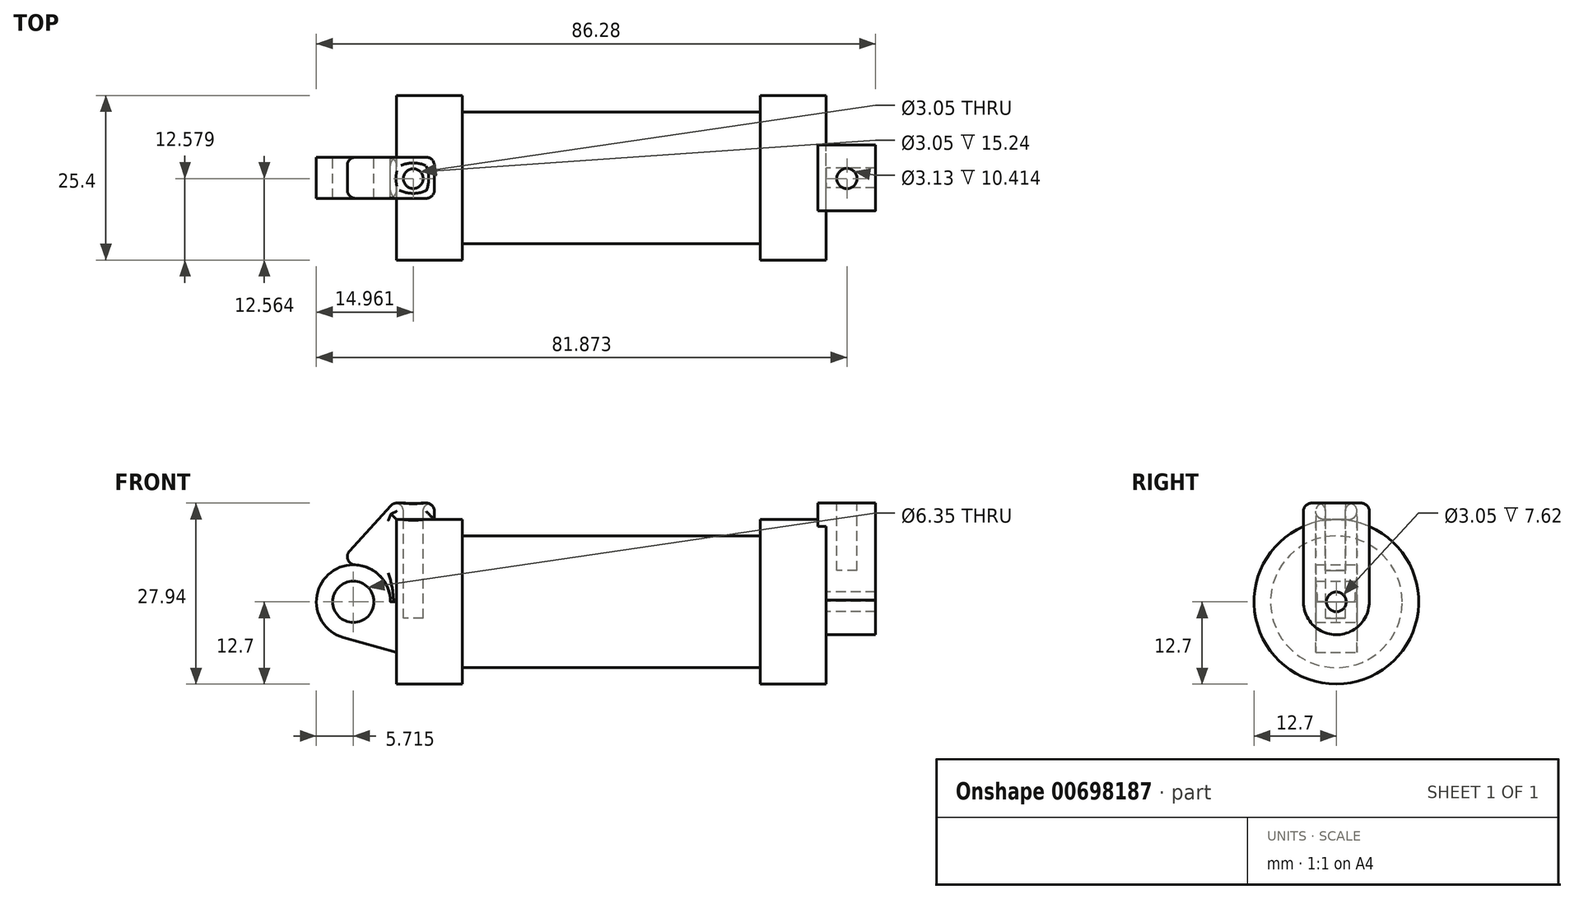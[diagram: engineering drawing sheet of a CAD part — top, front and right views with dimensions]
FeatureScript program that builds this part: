
annotation { "Feature Type Name" : "Feature", "Feature Type Description" : "" }
export const myFeature = defineFeature(function(context is Context, id is Id, definition is map)
    precondition{}
    {
        {
            var Q0;
            Q0=qCreatedBy(makeId("Front.planeOp"),FACE);
            var sketch = newSketch(context, id + "F0", { "sketchPlane" : qUnion([Q0])});
            skLineSegment(sketch, "E0", {"start": v(0, 0) * mm, "end": v(0, 12.7) * mm});
            skLineSegment(sketch, "E1", {"start": v(0, 12.7) * mm, "end": v(10.16, 12.7) * mm});
            skLineSegment(sketch, "E2", {"start": v(10.16, 12.7) * mm, "end": v(10.16, 10.16) * mm});
            skLineSegment(sketch, "E3", {"start": v(10.16, 10.16) * mm, "end": v(56.13, 10.16) * mm});
            skLineSegment(sketch, "E4", {"start": v(56.13, 10.16) * mm, "end": v(56.13, 12.7) * mm});
            skLineSegment(sketch, "E5", {"start": v(56.13, 12.7) * mm, "end": v(66.3, 12.7) * mm});
            skLineSegment(sketch, "E6", {"start": v(66.3, 12.7) * mm, "end": v(66.3, 0) * mm});
            skLineSegment(sketch, "E7", {"start": v(66.3, 0) * mm, "end": v(0, 0) * mm});
            skLineSegment(sketch, "E8", {"start": v(5.84, 15.24) * mm, "end": v(-0.5, 15.24) * mm});
            skLineSegment(sketch, "E9", {"start": v(-0.5, 15.24) * mm, "end": v(-10.88, 3.85) * mm});
            skLineSegment(sketch, "E10", {"start": v(0, 0) * mm, "end": v(-6.65, 0) * mm});
            skCircle(sketch, "E11", {"center": v(-6.65, 0) * mm, "radius": 5.72 * mm});
            skCircle(sketch, "E12", {"center": v(-6.65, 0) * mm, "radius": 3.18 * mm});
            skLineSegment(sketch, "E13", {"start": v(5.84, 15.24) * mm, "end": v(5.84, -9.4) * mm});
            skLineSegment(sketch, "E14", {"start": v(5.84, -9.4) * mm, "end": v(-8.18, -5.5) * mm});
            skSolve(sketch);
        }
        {
            var Q0;
            {var subQ0=sQuery(id+"F0.wireOp",EDGE,"E2");Q0=makeQuery(id+"F0.imprint","IMPRINT",FACE,{"disambiguationData":[TD([[makeQuery(id+"F0.imprint","IMPRINT",EDGE,{"derivedFrom":subQ0}),-1.0]])]});}
            var Q1;
            {var subQ0=sQuery(id+"F0.wireOp",EDGE,"E0");Q1=makeQuery(id+"F0.imprint","IMPRINT",FACE,{"disambiguationData":[TD([[makeQuery(id+"F0.imprint","IMPRINT",EDGE,{"derivedFrom":subQ0}),-1.0]])]});}
            var Q2;
            Q2=sQuery(id+"F0.wireOp",EDGE,"E7");
            revolve(context, id + "F1", {"entities" : qUnion([Q0, Q1]), "axis" : qUnion([Q2]), "revolveType" : RevolveType.FULL});
        }
        {
            var Q0;
            {var subQ5=sQuery(id+"F0.wireOp",EDGE,"E12");Q0=makeQuery(id+"F0.imprint","IMPRINT",FACE,{"disambiguationData":[TD([[makeQuery(id+"F0.imprint","IMPRINT",EDGE,{"derivedFrom":subQ5}),-1.0]])]});}
            var Q1;
            {var subQ0=sQuery(id+"F0.wireOp",EDGE,"E14");Q1=makeQuery(id+"F0.imprint","IMPRINT",FACE,{"disambiguationData":[TD([[makeQuery(id+"F0.imprint","IMPRINT",EDGE,{"derivedFrom":subQ0}),-1.0]])]});}
            extrude(context, id + "F2", {"entities" : qUnion([Q0, Q1]), "operationType" : NewBodyOperationType.ADD, "endBound" : BoundingType.SYMMETRIC, "depth" : 6.35 * mm, "offsetDistance" : 25.4 * mm});
        }
        {
            var Q0;
            {var subQ1=sQuery(id+"F0.wireOp",EDGE,"E0");Q0=makeQuery(id+"F0.imprint","IMPRINT",FACE,{"disambiguationData":[TD([[makeQuery(id+"F0.imprint","IMPRINT",EDGE,{"derivedFrom":subQ1}),1.0]])]});}
            extrude(context, id + "F3", {"entities" : qUnion([Q0]), "endBound" : BoundingType.SYMMETRIC, "depth" : 6.35 * mm, "offsetDistance" : 25.4 * mm});
        }
        {
            var Q0;
            Q0=makeQuery(id+"F1.opRevolve","SWEPT_FACE",FACE,{"disambiguationData":[OSD([sQuery(id+"F0.wireOp",EDGE,"E6")])]});
            var sketch = newSketch(context, id + "F4", { "sketchPlane" : qUnion([Q0])});
            skCircle(sketch, "E15", {"center": v(0, 0) * mm, "radius": 1.52 * mm});
            skCircle(sketch, "E16", {"center": v(0, 0) * mm, "radius": 5.08 * mm});
            skLineSegment(sketch, "E17", {"start": v(-5.07, 0.25) * mm, "end": v(-5.07, 13.97) * mm});
            skLineSegment(sketch, "E18", {"start": v(5.08, 0.05) * mm, "end": v(5.08, 13.97) * mm});
            skLineSegment(sketch, "E19", {"start": v(-3.8, 15.24) * mm, "end": v(3.8, 15.24) * mm});
            skPoint(sketch, "E20.visualSharp", {"position": v(-5.07, 15.24) * mm});
            skArc(sketch, "E20.filletArc", {"start": v(-3.8, 15.24) * mm, "mid": v(-4.7, 14.87) * mm, "end": v(-5.07, 13.97) * mm});
            skPoint(sketch, "E21.visualSharp", {"position": v(5.08, 15.24) * mm});
            skArc(sketch, "E21.filletArc", {"start": v(5.08, 13.97) * mm, "mid": v(4.7, 14.87) * mm, "end": v(3.8, 15.24) * mm});
            skSolve(sketch);
        }
        {
            var Q0;
            Q0=makeQuery(id+"F4.imprint","IMPRINT",FACE,{"disambiguationData":[TD([[makeQuery(id+"F4.imprint","IMPRINT",EDGE,{"derivedFrom":sQuery(id+"F4.wireOp",EDGE,"E15")}),-1.0]])]});
            var Q1;
            {var subQ0=sQuery(id+"F4.wireOp",EDGE,"E17");var subQ1=sQuery(id+"F4.wireOp",EDGE,"E16");var subQ2=makeQuery(id+"F4.imprint","INTERSECT",VERTEX,{"derivedFrom":[subQ1,subQ0]});Q1=makeQuery(id+"F4.imprint","IMPRINT",FACE,{"disambiguationData":[TD([[makeQuery(id+"F4.imprint","IMPRINT",EDGE,{"disambiguationData":[TD([[subQ2,1.0]])],"derivedFrom":subQ1}),-1.0]])]});}
            extrude(context, id + "F5", {"entities" : qUnion([Q0, Q1]), "operationType" : NewBodyOperationType.ADD, "depth" : 7.62 * mm, "offsetDistance" : 25.4 * mm});
        }
        {
            var Q0;
            {var subQ0=sQuery(id+"F4.wireOp",EDGE,"E19");Q0=makeQuery(id+"F4.imprint","IMPRINT",FACE,{"disambiguationData":[TD([[makeQuery(id+"F4.imprint","IMPRINT",EDGE,{"derivedFrom":subQ0}),-1.0]])]});}
            extrude(context, id + "F6", {"entities" : qUnion([Q0]), "operationType" : NewBodyOperationType.ADD, "depth" : 7.62 * mm, "offsetDistance" : 25.4 * mm, "hasSecondDirection" : true, "secondDirectionOppositeDirection" : true, "secondDirectionDepth" : 1.27 * mm});
        }
        {
            var Q0;
            Q0=makeQuery(id+"F3.opExtrude","SWEPT_FACE",FACE,{"disambiguationData":[OSD([sQuery(id+"F0.wireOp",EDGE,"E8")])]});
            var sketch = newSketch(context, id + "F7", { "sketchPlane" : qUnion([Q0])});
            skCircle(sketch, "E22", {"center": v(2.6, -0.14) * mm, "radius": 1.52 * mm});
            skCircle(sketch, "E23", {"center": v(69.74, 0.16) * mm, "radius": 1.52 * mm});
            skSolve(sketch);
        }
        {
            var Q0;
            Q0=makeQuery(id+"F7.imprint","IMPRINT",FACE,{"disambiguationData":[TD([[makeQuery(id+"F7.imprint","IMPRINT",EDGE,{"derivedFrom":sQuery(id+"F7.wireOp",EDGE,"E22")}),1.0]])]});
            extrude(context, id + "F8", {"entities" : qUnion([Q0]), "operationType" : NewBodyOperationType.REMOVE, "oppositeDirection" : true, "depth" : 17.78 * mm, "offsetDistance" : 25.4 * mm});
        }
        {
            var Q0;
            Q0=makeQuery(id+"F6.opExtrude","SWEPT_FACE",FACE,{"disambiguationData":[OSD([sQuery(id+"F4.wireOp",EDGE,"E19")])]});
            var sketch = newSketch(context, id + "F9", { "sketchPlane" : qUnion([Q0])});
            skCircle(sketch, "E24", {"center": v(69.5, -0.12) * mm, "radius": 1.57 * mm});
            skSolve(sketch);
        }
        {
            var Q0;
            Q0 = qSketchRegion(id + "F9", true);
            extrude(context, id + "F10", {"entities" : qUnion([Q0]), "operationType" : NewBodyOperationType.REMOVE, "oppositeDirection" : true, "depth" : 10.4 * mm, "offsetDistance" : 25.4 * mm});
        }
        {
            var Q0;
            Q0=makeQuery(id+"F1.opRevolve","SWEPT_FACE",FACE,{"disambiguationData":[OSD([sQuery(id+"F0.wireOp",EDGE,"E2")])]});
            var Q1;
            Q1=makeQuery(id+"F1.opRevolve","SWEPT_FACE",FACE,{"disambiguationData":[OSD([sQuery(id+"F0.wireOp",EDGE,"E3")])]});
            var Q2;
            Q2=makeQuery(id+"F1.opRevolve","SWEPT_EDGE",EDGE,{"disambiguationData":[OSD([sQuery(id+"F0.wireOp",EDGE,"E5"),sQuery(id+"F0.wireOp",EDGE,"E6")])]});
            var Q3;
            Q3=makeQuery(id+"F1.opRevolve","SWEPT_EDGE",EDGE,{"disambiguationData":[OSD([sQuery(id+"F0.wireOp",EDGE,"E4"),sQuery(id+"F0.wireOp",EDGE,"E5")])]});
            var Q4;
            {var subQ0=sQuery(id+"F4.wireOp",EDGE,"E18");var subQ1=sQuery(id+"F4.wireOp",EDGE,"E17");var subQ2=sQuery(id+"F0.wireOp",EDGE,"E6");var subQ3=sQuery(id+"F0.wireOp",EDGE,"E5");Q4=makeQuery(id+"F6.boolean.opBoolean","MERGE",FACE,{"derivedFrom":[makeQuery(id+"F5.opExtrude","CAP_FACE",FACE,{"disambiguationData":[OSD([subQ3,subQ2,sQuery(id+"F4.wireOp",EDGE,"E15"),sQuery(id+"F4.wireOp",EDGE,"E16"),subQ1,subQ0])],"isStart":false}),makeQuery(id+"F6.opExtrude","CAP_FACE",FACE,{"disambiguationData":[OSD([subQ3,subQ2,subQ1,subQ0,sQuery(id+"F4.wireOp",EDGE,"E19"),sQuery(id+"F4.wireOp",EDGE,"E20.filletArc"),sQuery(id+"F4.wireOp",EDGE,"E21.filletArc")])],"isStart":false})]});}
            var Q5;
            Q5=makeQuery(id+"F1.opRevolve","SWEPT_FACE",FACE,{"disambiguationData":[OSD([sQuery(id+"F0.wireOp",EDGE,"E1")])]});
            var Q6;
            Q6=makeQuery(id+"F3.opExtrude","SWEPT_FACE",FACE,{"disambiguationData":[OSD([sQuery(id+"F0.wireOp",EDGE,"E9")])]});
            var Q7;
            Q7=makeQuery(id+"F3.opExtrude","SWEPT_FACE",FACE,{"disambiguationData":[OSD([sQuery(id+"F0.wireOp",EDGE,"E8")])]});
            var Q8;
            Q8=makeQuery(id+"F6.opExtrude","CAP_FACE",FACE,{"disambiguationData":[OSD([sQuery(id+"F0.wireOp",EDGE,"E5"),sQuery(id+"F0.wireOp",EDGE,"E6"),sQuery(id+"F4.wireOp",EDGE,"E17"),sQuery(id+"F4.wireOp",EDGE,"E18"),sQuery(id+"F4.wireOp",EDGE,"E19"),sQuery(id+"F4.wireOp",EDGE,"E20.filletArc"),sQuery(id+"F4.wireOp",EDGE,"E21.filletArc")])],"isStart":true});
            var Q9;
            Q9=makeQuery(id+"F6.opExtrude","SWEPT_FACE",FACE,{"disambiguationData":[OSD([sQuery(id+"F4.wireOp",EDGE,"E19")])]});
            var Q10;
            Q10=makeQuery(id+"F3.opExtrude","CAP_FACE",FACE,{"disambiguationData":[OSD([sQuery(id+"F0.wireOp",EDGE,"E0"),sQuery(id+"F0.wireOp",EDGE,"E1"),sQuery(id+"F0.wireOp",EDGE,"E8"),sQuery(id+"F0.wireOp",EDGE,"E9"),sQuery(id+"F0.wireOp",EDGE,"E10"),sQuery(id+"F0.wireOp",EDGE,"E11"),sQuery(id+"F0.wireOp",EDGE,"E13")])],"isStart":true});
            var Q11;
            Q11=makeQuery(id+"F3.opExtrude","CAP_FACE",FACE,{"disambiguationData":[OSD([sQuery(id+"F0.wireOp",EDGE,"E0"),sQuery(id+"F0.wireOp",EDGE,"E1"),sQuery(id+"F0.wireOp",EDGE,"E8"),sQuery(id+"F0.wireOp",EDGE,"E9"),sQuery(id+"F0.wireOp",EDGE,"E10"),sQuery(id+"F0.wireOp",EDGE,"E11"),sQuery(id+"F0.wireOp",EDGE,"E13")])],"isStart":false});
            var Q12;
            Q12=makeQuery(id+"F2.opExtrude","CAP_EDGE",EDGE,{"disambiguationData":[OSD([sQuery(id+"F0.wireOp",EDGE,"E11")])],"isStart":false});
            var Q13;
            Q13=makeQuery(id+"F2.opExtrude","CAP_EDGE",EDGE,{"disambiguationData":[OSD([sQuery(id+"F0.wireOp",EDGE,"E11")])],"isStart":true});
            var Q14;
            {var subQ0=sQuery(id+"F0.wireOp",EDGE,"E5");Q14=makeQuery(id+"F5.boolean.opBoolean","MERGE",FACE,{"derivedFrom":[makeQuery(id+"F1.opRevolve","SWEPT_FACE",FACE,{"disambiguationData":[OSD([subQ0])]}),makeQuery(id+"F5.opExtrude","SWEPT_FACE",FACE,{"disambiguationData":[OSD([subQ0,sQuery(id+"F0.wireOp",EDGE,"E6")])]})]});}
            var Q15;
            Q15=makeQuery(id+"F1.opRevolve","SWEPT_FACE",FACE,{"disambiguationData":[OSD([sQuery(id+"F0.wireOp",EDGE,"E4")])]});
            fillet(context, id + "F11", {"entities" : qUnion([Q0, Q1, Q2, Q3, Q4, Q5, Q6, Q7, Q8, Q9, Q10, Q11, Q12, Q13, Q14, Q15]), "radius" : 1.27 * mm, "tangentPropagation" : true, "allowEdgeOverflow" : false});
        }
    });
